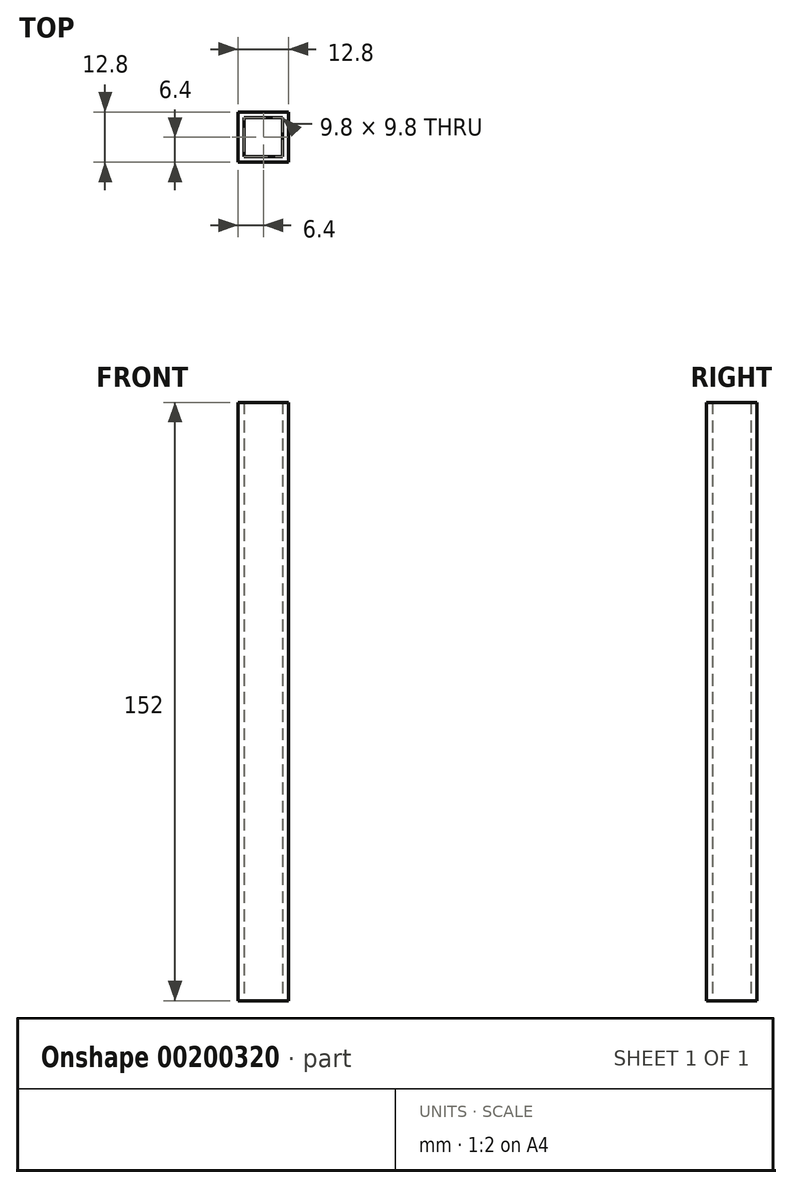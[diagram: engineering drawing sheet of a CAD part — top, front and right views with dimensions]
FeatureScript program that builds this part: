
annotation { "Feature Type Name" : "Feature", "Feature Type Description" : "" }
export const myFeature = defineFeature(function(context is Context, id is Id, definition is map)
    precondition{}
    {
        {
            var Q0;
            Q0=qCreatedBy(makeId("Top.planeOp"),FACE);
            var sketch = newSketch(context, id + "F0", { "sketchPlane" : qUnion([Q0])});
            skPoint(sketch, "E0.middle", {"position": v(0, 0) * mm});
            skLineSegment(sketch, "E1.bottom", {"start": v(-6.4, -6.4) * mm, "end": v(6.4, -6.4) * mm});
            skLineSegment(sketch, "E1.top", {"start": v(-6.4, 6.4) * mm, "end": v(6.4, 6.4) * mm});
            skLineSegment(sketch, "E1.left", {"start": v(-6.4, -6.4) * mm, "end": v(-6.4, 6.4) * mm});
            skLineSegment(sketch, "E1.right", {"start": v(6.4, -6.4) * mm, "end": v(6.4, 6.4) * mm});
            skLineSegment(sketch, "E2.bottom", {"start": v(-6.4, -6.4) * mm, "end": v(-4.9, -6.4) * mm, "construction": true});
            skLineSegment(sketch, "E2.top", {"start": v(-6.4, -4.9) * mm, "end": v(-4.9, -4.9) * mm, "construction": true});
            skLineSegment(sketch, "E2.left", {"start": v(-6.4, -6.4) * mm, "end": v(-6.4, -4.9) * mm, "construction": true});
            skLineSegment(sketch, "E2.right", {"start": v(-4.9, -6.4) * mm, "end": v(-4.9, -4.9) * mm, "construction": true});
            skLineSegment(sketch, "E3.bottom", {"start": v(6.4, 6.4) * mm, "end": v(4.9, 6.4) * mm, "construction": true});
            skLineSegment(sketch, "E3.top", {"start": v(6.4, 4.9) * mm, "end": v(4.9, 4.9) * mm, "construction": true});
            skLineSegment(sketch, "E3.left", {"start": v(6.4, 6.4) * mm, "end": v(6.4, 4.9) * mm, "construction": true});
            skLineSegment(sketch, "E3.right", {"start": v(4.9, 6.4) * mm, "end": v(4.9, 4.9) * mm, "construction": true});
            skLineSegment(sketch, "E4.bottom", {"start": v(-4.9, -4.9) * mm, "end": v(4.9, -4.9) * mm});
            skLineSegment(sketch, "E4.top", {"start": v(-4.9, 4.9) * mm, "end": v(4.9, 4.9) * mm});
            skLineSegment(sketch, "E4.left", {"start": v(-4.9, -4.9) * mm, "end": v(-4.9, 4.9) * mm});
            skLineSegment(sketch, "E4.right", {"start": v(4.9, -4.9) * mm, "end": v(4.9, 4.9) * mm});
            skSolve(sketch);
        }
        {
            var Q0;
            Q0=makeQuery(id+"F0.imprint","IMPRINT",FACE,{"disambiguationData":[TD([[makeQuery(id+"F0.imprint","IMPRINT",EDGE,{"derivedFrom":sQuery(id+"F0.wireOp",EDGE,"E1.bottom")}),1.0]])]});
            extrude(context, id + "F1", {"entities" : qUnion([Q0]), "depth" : 152 * mm});
        }
    });
